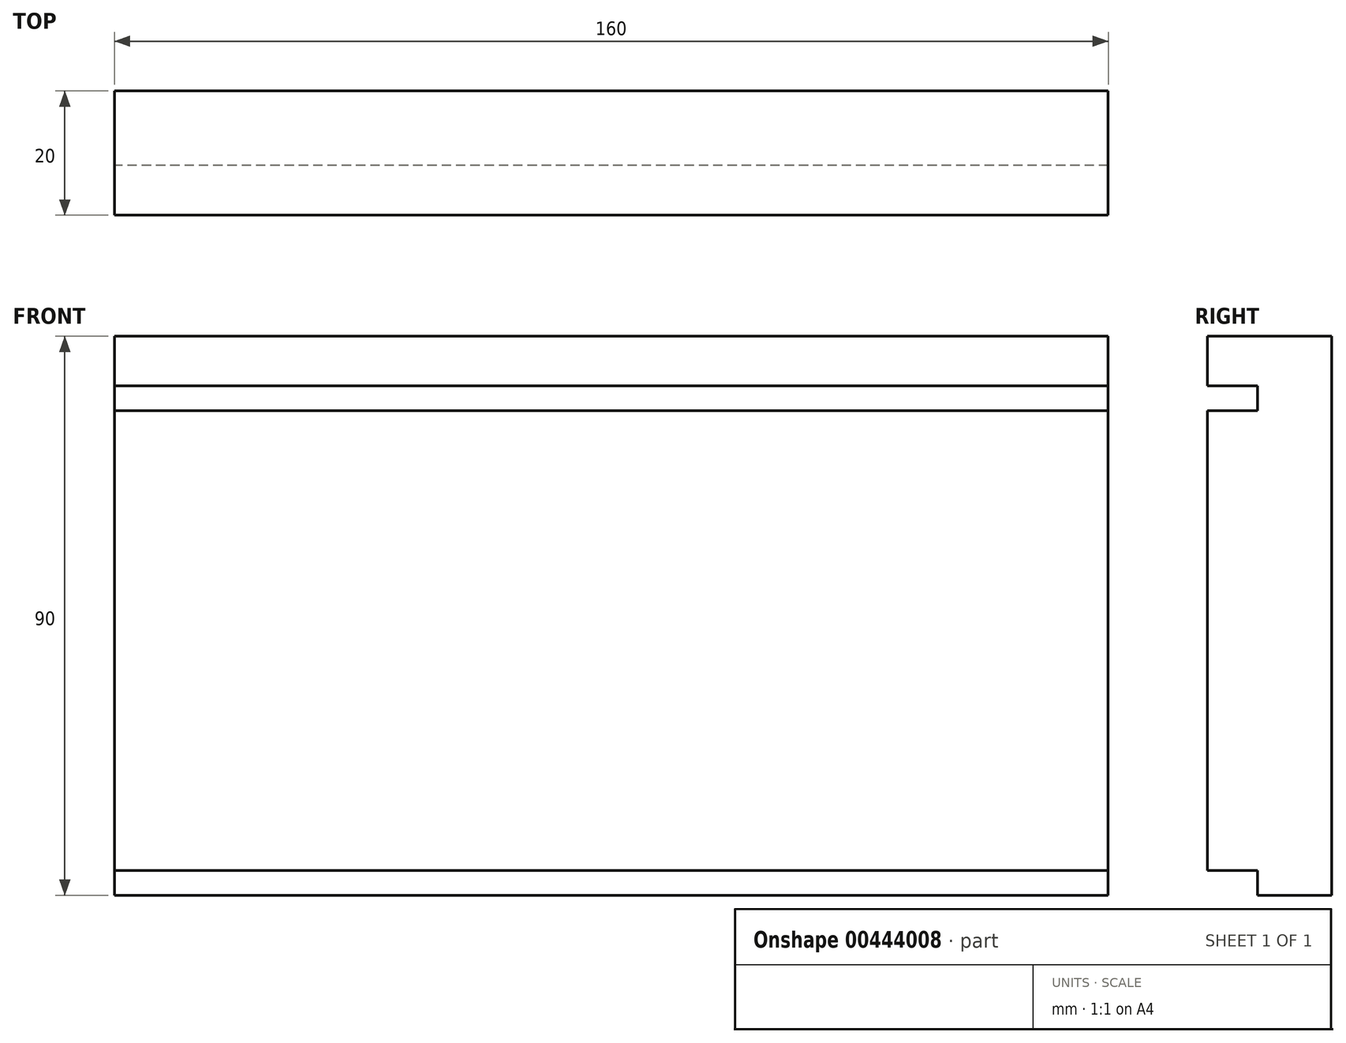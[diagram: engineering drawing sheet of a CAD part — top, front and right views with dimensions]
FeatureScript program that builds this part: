
annotation { "Feature Type Name" : "Feature", "Feature Type Description" : "" }
export const myFeature = defineFeature(function(context is Context, id is Id, definition is map)
    precondition{}
    {
        {
            var Q0;
            Q0=qCreatedBy(makeId("Front.planeOp"),FACE);
            var sketch = newSketch(context, id + "F0", { "sketchPlane" : qUnion([Q0])});
            skLineSegment(sketch, "E0.bottom", {"start": v(73.13, 42.33) * mm, "end": v(-86.87, 42.33) * mm});
            skLineSegment(sketch, "E0.top", {"start": v(73.13, -47.67) * mm, "end": v(-86.87, -47.67) * mm});
            skLineSegment(sketch, "E0.left", {"start": v(73.13, 42.33) * mm, "end": v(73.13, -47.67) * mm});
            skLineSegment(sketch, "E0.right", {"start": v(-86.87, 42.33) * mm, "end": v(-86.87, -47.67) * mm});
            skLineSegment(sketch, "E1", {"start": v(73.13, 34.33) * mm, "end": v(-86.87, 34.33) * mm});
            skLineSegment(sketch, "E2", {"start": v(73.13, 30.33) * mm, "end": v(-86.87, 30.33) * mm});
            skLineSegment(sketch, "E3", {"start": v(73.13, -43.67) * mm, "end": v(-86.87, -43.67) * mm});
            skSolve(sketch);
        }
        {
            var Q0;
            {var subQ0=sQuery(id+"F0.wireOp",EDGE,"E2");Q0=makeQuery(id+"F0.imprint","IMPRINT",FACE,{"disambiguationData":[TD([[makeQuery(id+"F0.imprint","IMPRINT",EDGE,{"derivedFrom":subQ0}),1.0]])]});}
            extrude(context, id + "F1", {"entities" : qUnion([Q0]), "depth" : 20 * mm});
        }
        {
            var Q0;
            {var subQ0=sQuery(id+"F0.wireOp",EDGE,"E0.top");Q0=makeQuery(id+"F0.imprint","IMPRINT",FACE,{"disambiguationData":[TD([[makeQuery(id+"F0.imprint","IMPRINT",EDGE,{"derivedFrom":subQ0}),-1.0]])]});}
            extrude(context, id + "F2", {"entities" : qUnion([Q0]), "operationType" : NewBodyOperationType.ADD, "depth" : 12 * mm});
        }
        {
            var Q0;
            {var subQ0=sQuery(id+"F0.wireOp",EDGE,"E1");Q0=makeQuery(id+"F0.imprint","IMPRINT",FACE,{"disambiguationData":[TD([[makeQuery(id+"F0.imprint","IMPRINT",EDGE,{"derivedFrom":subQ0}),1.0]])]});}
            extrude(context, id + "F3", {"entities" : qUnion([Q0]), "operationType" : NewBodyOperationType.ADD, "depth" : 12 * mm});
        }
        {
            var Q0;
            {var subQ0=sQuery(id+"F0.wireOp",EDGE,"E0.bottom");Q0=makeQuery(id+"F0.imprint","IMPRINT",FACE,{"disambiguationData":[TD([[makeQuery(id+"F0.imprint","IMPRINT",EDGE,{"derivedFrom":subQ0}),1.0]])]});}
            extrude(context, id + "F4", {"entities" : qUnion([Q0]), "operationType" : NewBodyOperationType.ADD, "depth" : 20 * mm});
        }
        {
            var Q0;
            {var subQ0=sQuery(id+"F0.wireOp",EDGE,"E1");Q0=makeQuery(id+"F0.imprint","IMPRINT",FACE,{"disambiguationData":[TD([[makeQuery(id+"F0.imprint","IMPRINT",EDGE,{"derivedFrom":subQ0}),1.0]])]});}
            extrude(context, id + "F5", {"entities" : qUnion([Q0]), "operationType" : NewBodyOperationType.ADD, "depth" : 12 * mm});
        }
        {
            var Q0;
            {var subQ0=sQuery(id+"F0.wireOp",EDGE,"E0.top");Q0=makeQuery(id+"F0.imprint","IMPRINT",FACE,{"disambiguationData":[TD([[makeQuery(id+"F0.imprint","IMPRINT",EDGE,{"derivedFrom":subQ0}),-1.0]])]});}
            extrude(context, id + "F6", {"entities" : qUnion([Q0]), "operationType" : NewBodyOperationType.ADD, "depth" : 12 * mm});
        }
        {
            var Q0;
            {var subQ0=sQuery(id+"F0.wireOp",EDGE,"E1");Q0=makeQuery(id+"F0.imprint","IMPRINT",FACE,{"disambiguationData":[TD([[makeQuery(id+"F0.imprint","IMPRINT",EDGE,{"derivedFrom":subQ0}),1.0]])]});}
            extrude(context, id + "F7", {"entities" : qUnion([Q0]), "operationType" : NewBodyOperationType.ADD, "depth" : 12 * mm});
        }
    });
